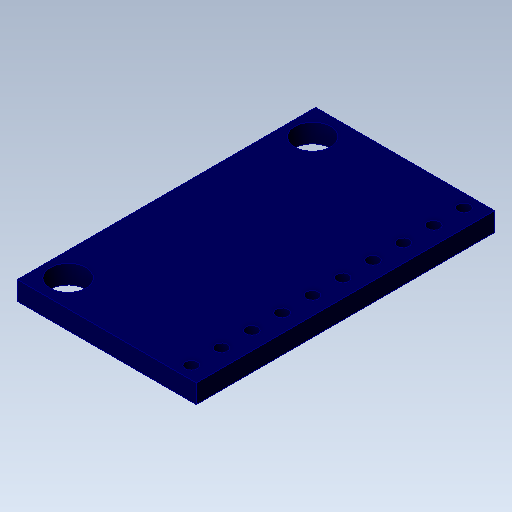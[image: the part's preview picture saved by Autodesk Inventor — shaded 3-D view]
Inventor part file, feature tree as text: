
AUTODESK INVENTOR PART (.ipt)
format: ipt  version: 2020.3 (Build 243373000, 373)  size: 138,240 bytes
history: native  units: mm
features: extrude x1, sketch x1
ambient origin geometry x8: Origin, YZ Plane, XZ Plane, XY Plane, X Axis, Y Axis, Z Axis, Center Point
bodies: Body1 (feature_tree)
feature tree (2):
  extrude  "Extrusion2"  Depth=25.0mm
  sketch  "Sketch1"  dims[d0=15.0mm d1=25.0mm d2=3.0mm d3=2.25mm d4=3.0mm d5=20.5mm d6=2.25mm d7=2.0mm d8=2.0mm d11=1.5mm d12=1.0mm d13=1.07mm d14=100.0mm d16=2.54mm d17=10.0mm d19=10.0mm d21=1.07mm d22=1.57mm d23=0.0mm]
